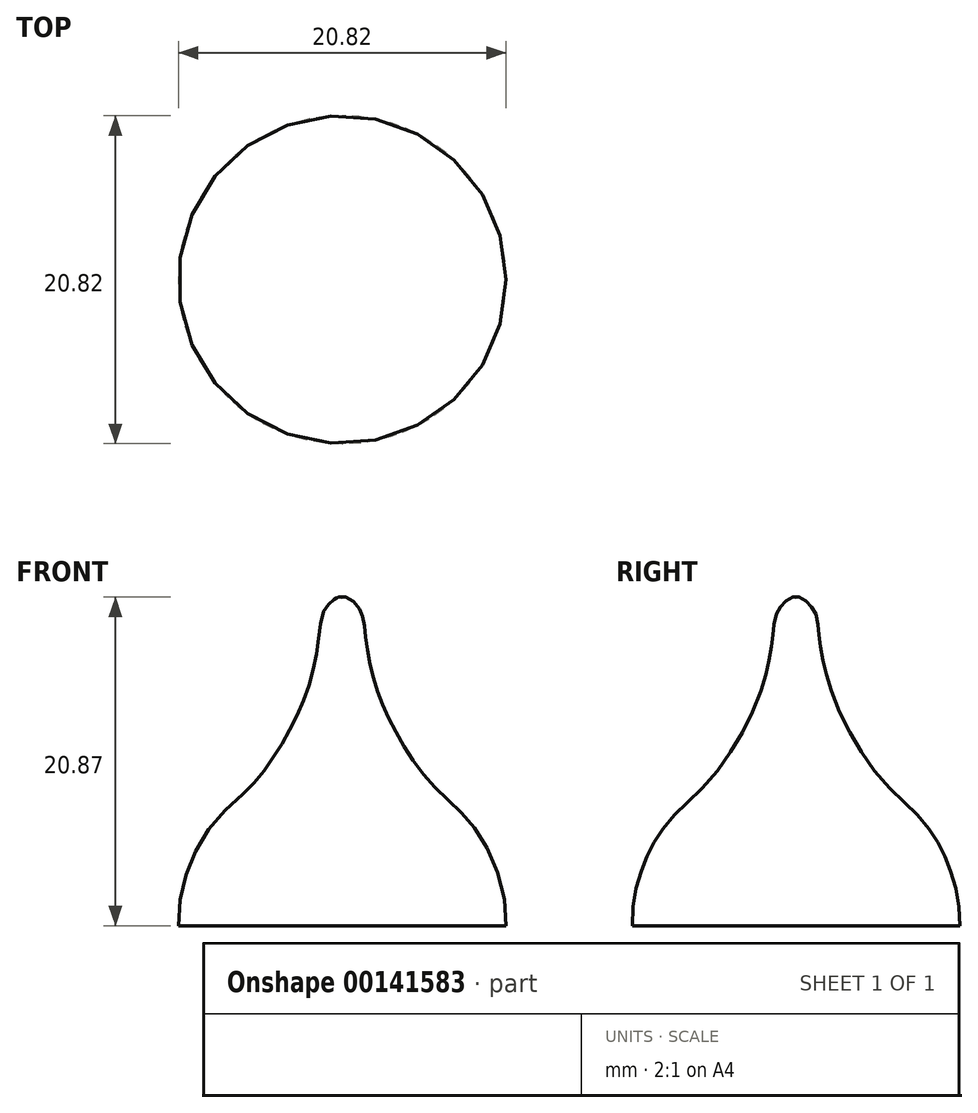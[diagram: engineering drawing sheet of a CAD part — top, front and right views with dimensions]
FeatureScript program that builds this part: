
annotation { "Feature Type Name" : "Feature", "Feature Type Description" : "" }
export const myFeature = defineFeature(function(context is Context, id is Id, definition is map)
    precondition{}
    {
        {
            var Q0;
            Q0=qCreatedBy(makeId("Front.planeOp"),FACE);
            var sketch = newSketch(context, id + "F0", { "sketchPlane" : qUnion([Q0])});
            skLineSegment(sketch, "E0", {"start": v(0, 20.8) * mm, "end": v(0, 0) * mm});
            skLineSegment(sketch, "E1", {"start": v(0, 0) * mm, "end": v(10.4, 0) * mm});
            skFitSpline(sketch, "E2", {"points": [v(0, 20.8) * mm, v(-1.86, 11) * mm, v(-3.3, 7.36) * mm, v(-7.28, 4.09) * mm, v(-8.1, -1.6) * mm, v(0.23, -2.88) * mm, v(9.8, -1.85) * mm, v(9.04, 5.24) * mm, v(5.97, 8.7) * mm, v(3.84, 11.53) * mm, v(2.54, 14.1) * mm, v(1.82, 16.36) * mm, v(1.45, 18.57) * mm, v(1.28, 19.7) * mm, v(0.8, 20.49) * mm, v(0, 20.8) * mm]});
            skLineSegment(sketch, "E3", {"start": v(0, 20.8) * mm, "end": v(0, 20.8) * mm});
            skSolve(sketch);
        }
        {
            var Q0;
            Q0=makeQuery(id+"F0.imprint","IMPRINT",FACE,{"disambiguationData":[TD([[makeQuery(id+"F0.imprint","IMPRINT",EDGE,{"derivedFrom":sQuery(id+"F0.wireOp",EDGE,"E0")}),1.0]])]});
            var Q1;
            Q1=sQuery(id+"F0.wireOp",EDGE,"E0");
            revolve(context, id + "F1", {"entities" : qUnion([Q0]), "axis" : qUnion([Q1]), "revolveType" : RevolveType.FULL});
        }
    });
